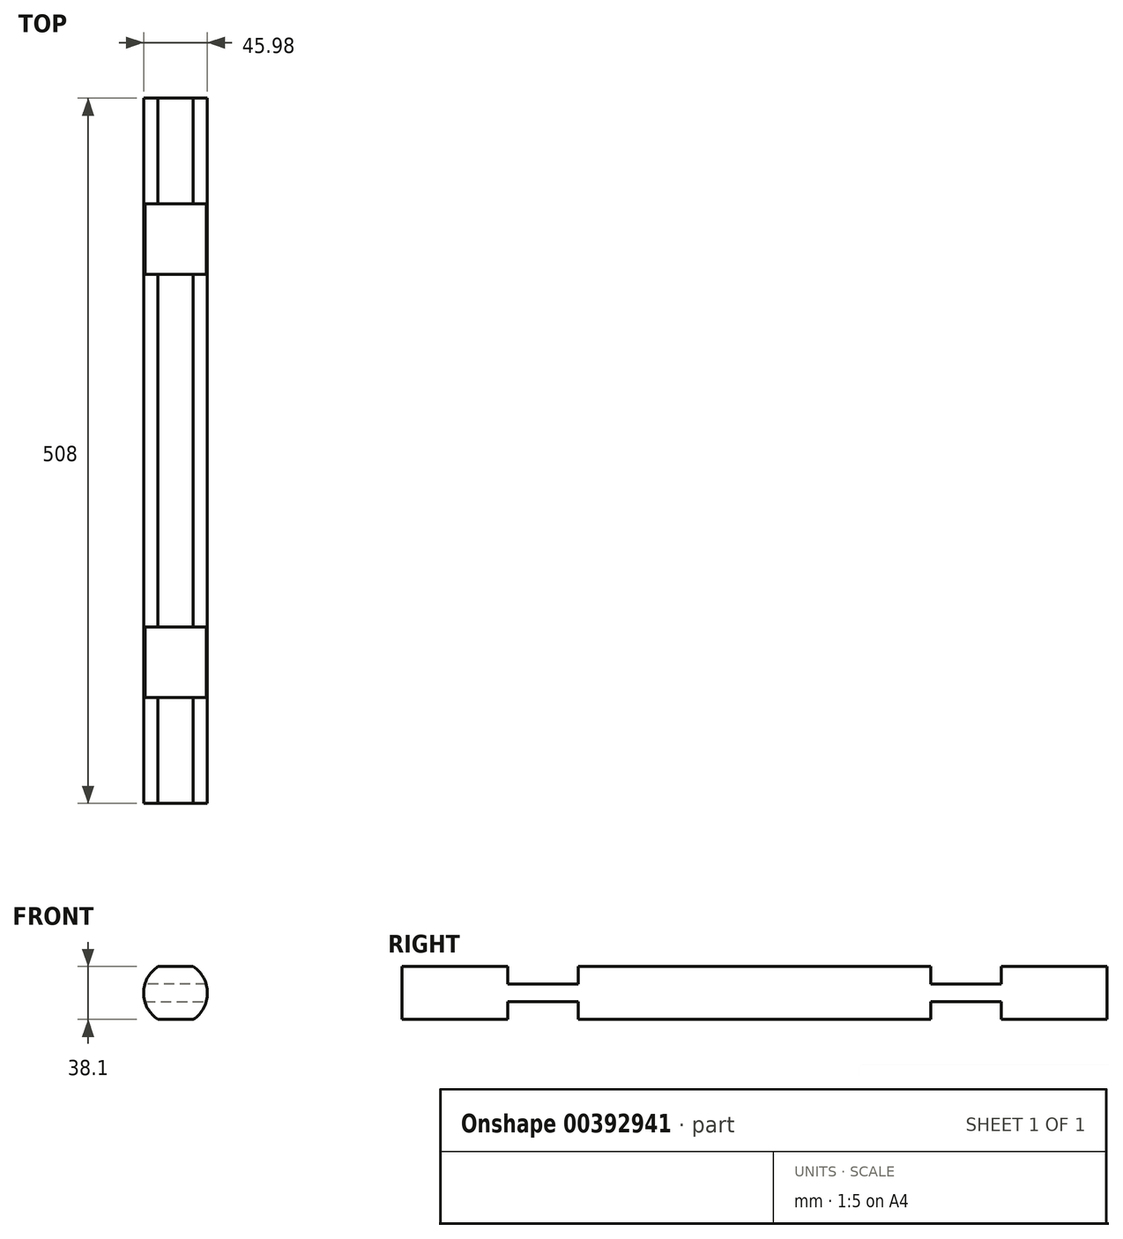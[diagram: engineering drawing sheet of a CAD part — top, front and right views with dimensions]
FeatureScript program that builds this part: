
annotation { "Feature Type Name" : "Feature", "Feature Type Description" : "" }
export const myFeature = defineFeature(function(context is Context, id is Id, definition is map)
    precondition{}
    {
        {
            var Q0;
            Q0=qCreatedBy(makeId("Front.planeOp"),FACE);
            var sketch = newSketch(context, id + "F0", { "sketchPlane" : qUnion([Q0])});
            skLineSegment(sketch, "E0", {"start": v(-21.85, 42.5) * mm, "end": v(3.55, 42.5) * mm});
            skLineSegment(sketch, "E1", {"start": v(-21.85, 4.4) * mm, "end": v(3.55, 4.4) * mm});
            skArc(sketch, "E2", {"start": v(-21.85, 42.5) * mm, "mid": v(-32.27, 23.45) * mm, "end": v(-21.85, 4.4) * mm});
            skArc(sketch, "E3", {"start": v(3.55, 4.4) * mm, "mid": v(13.71, 23.45) * mm, "end": v(3.55, 42.5) * mm});
            skSolve(sketch);
        }
        {
            var Q0;
            Q0=qSketchRegion(id+"F0",true);
            extrude(context, id + "F1", {"entities" : qUnion([Q0]), "depth" : 508 * mm});
        }
        {
            var Q0;
            Q0=makeQuery(id+"F1.opExtrude","SWEPT_FACE",FACE,{"disambiguationData":[OSD([sQuery(id+"F0.wireOp",EDGE,"E0")])]});
            var sketch = newSketch(context, id + "F2", { "sketchPlane" : qUnion([Q0])});
            skLineSegment(sketch, "E4.bottom", {"start": v(-49.32, -431.8) * mm, "end": v(31.02, -431.8) * mm});
            skLineSegment(sketch, "E4.top", {"start": v(-49.32, -381) * mm, "end": v(31.02, -381) * mm});
            skLineSegment(sketch, "E4.left", {"start": v(-49.32, -431.8) * mm, "end": v(-49.32, -381) * mm});
            skLineSegment(sketch, "E4.right", {"start": v(31.02, -431.8) * mm, "end": v(31.02, -381) * mm});
            skPoint(sketch, "E4.middle", {"position": v(-9.15, -406.4) * mm});
            skPoint(sketch, "E4.middle.positionSnap0", {"position": v(-9.15, -508) * mm});
            skPoint(sketch, "E4.centerSnap0", {"position": v(-9.15, -508) * mm});
            skLineSegment(sketch, "E5.bottom", {"start": v(32.29, -127) * mm, "end": v(-50.58, -127) * mm});
            skLineSegment(sketch, "E5.top", {"start": v(32.29, -76.2) * mm, "end": v(-50.58, -76.2) * mm});
            skLineSegment(sketch, "E5.left", {"start": v(32.29, -127) * mm, "end": v(32.29, -76.2) * mm});
            skLineSegment(sketch, "E5.right", {"start": v(-50.58, -127) * mm, "end": v(-50.58, -76.2) * mm});
            skPoint(sketch, "E5.middle", {"position": v(-9.15, -101.6) * mm});
            skPoint(sketch, "E5.middle.positionSnap0", {"position": v(-9.15, 0) * mm});
            skPoint(sketch, "E5.centerSnap0", {"position": v(-9.15, 0) * mm});
            skSolve(sketch);
        }
        {
            var Q0;
            Q0=qSketchRegion(id+"F2",true);
            extrude(context, id + "F3", {"entities" : qUnion([Q0]), "operationType" : NewBodyOperationType.REMOVE, "oppositeDirection" : true, "depth" : 12.7 * mm});
        }
        {
            var Q0;
            Q0=makeQuery(id+"F1.opExtrude","SWEPT_FACE",FACE,{"disambiguationData":[OSD([sQuery(id+"F0.wireOp",EDGE,"E1")])]});
            var sketch = newSketch(context, id + "F4", { "sketchPlane" : qUnion([Q0])});
            skLineSegment(sketch, "E6.bottom", {"start": v(-51, 127) * mm, "end": v(32.7, 127) * mm});
            skLineSegment(sketch, "E6.top", {"start": v(-51, 76.2) * mm, "end": v(32.7, 76.2) * mm});
            skLineSegment(sketch, "E6.left", {"start": v(-51, 127) * mm, "end": v(-51, 76.2) * mm});
            skLineSegment(sketch, "E6.right", {"start": v(32.7, 127) * mm, "end": v(32.7, 76.2) * mm});
            skPoint(sketch, "E6.middle", {"position": v(-9.15, 101.6) * mm});
            skPoint(sketch, "E6.middle.positionSnap0", {"position": v(-9.15, 0) * mm});
            skPoint(sketch, "E6.centerSnap0", {"position": v(-9.15, 0) * mm});
            skLineSegment(sketch, "E7.bottom", {"start": v(-49.3, 431.8) * mm, "end": v(31, 431.8) * mm});
            skLineSegment(sketch, "E7.top", {"start": v(-49.3, 381) * mm, "end": v(31, 381) * mm});
            skLineSegment(sketch, "E7.left", {"start": v(-49.3, 431.8) * mm, "end": v(-49.3, 381) * mm});
            skLineSegment(sketch, "E7.right", {"start": v(31, 431.8) * mm, "end": v(31, 381) * mm});
            skPoint(sketch, "E7.middle", {"position": v(-9.15, 406.4) * mm});
            skPoint(sketch, "E7.middle.positionSnap0", {"position": v(-9.15, 508) * mm});
            skPoint(sketch, "E7.centerSnap0", {"position": v(-9.15, 508) * mm});
            skSolve(sketch);
        }
        {
            var Q0;
            Q0 = qSketchRegion(id + "F4", true);
            extrude(context, id + "F5", {"entities" : qUnion([Q0]), "operationType" : NewBodyOperationType.REMOVE, "oppositeDirection" : true, "depth" : 12.7 * mm});
        }
    });
